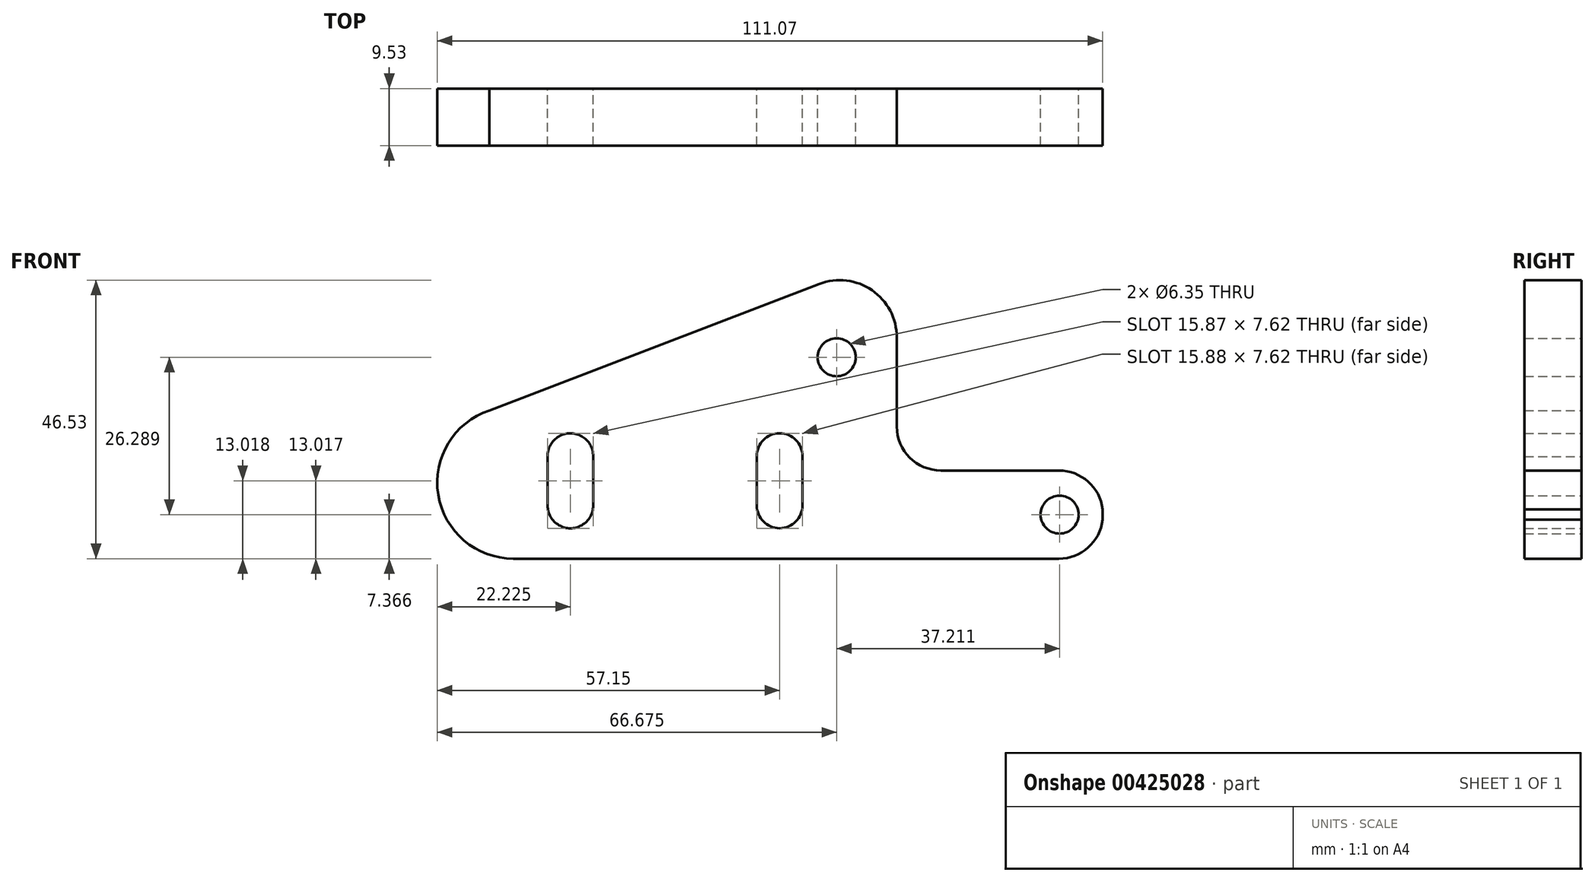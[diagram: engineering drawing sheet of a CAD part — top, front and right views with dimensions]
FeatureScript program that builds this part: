
annotation { "Feature Type Name" : "Feature", "Feature Type Description" : "" }
export const myFeature = defineFeature(function(context is Context, id is Id, definition is map)
    precondition{}
    {
        {
            var Q0;
            Q0=qCreatedBy(makeId("Front.planeOp"),FACE);
            var sketch = newSketch(context, id + "F0", { "sketchPlane" : qUnion([Q0])});
            skArc(sketch, "E0", {"start": v(-4, 12.06) * mm, "mid": v(-12.54, -2.02) * mm, "end": v(0, -12.7) * mm});
            skLineSegment(sketch, "E1", {"start": v(0, -12.7) * mm, "end": v(91.06, -12.7) * mm});
            skLineSegment(sketch, "E2", {"start": v(-5.1, 11.63) * mm, "end": v(51.07, 33.2) * mm});
            skArc(sketch, "E3", {"start": v(91.06, -12.7) * mm, "mid": v(98.43, -5.33) * mm, "end": v(91.06, 2.03) * mm});
            skLineSegment(sketch, "E4", {"start": v(-12.7, 37.63) * mm, "end": v(-12.7, -27.3) * mm, "construction": true});
            skLineSegment(sketch, "E5", {"start": v(98.43, 29.58) * mm, "end": v(98.43, -38.1) * mm, "construction": true});
            skLineSegment(sketch, "E6", {"start": v(91.06, 2.03) * mm, "end": v(71.37, 2.03) * mm});
            skArc(sketch, "E7", {"start": v(64, 9.4) * mm, "mid": v(66.17, 4.19) * mm, "end": v(71.37, 2.03) * mm});
            skLineSegment(sketch, "E8", {"start": v(64, 9.4) * mm, "end": v(64, 24.3) * mm});
            skLineSegment(sketch, "E9", {"start": v(71.37, 9.4) * mm, "end": v(64, 9.4) * mm, "construction": true});
            skPoint(sketch, "E10.visualSharp", {"position": v(64, 38.16) * mm});
            skArc(sketch, "E10.filletArc", {"start": v(64, 24.3) * mm, "mid": v(59.88, 32.15) * mm, "end": v(51.07, 33.2) * mm});
            skCircle(sketch, "E11", {"center": v(91.19, -5.33) * mm, "radius": 3.18 * mm});
            skCircle(sketch, "E12", {"center": v(53.98, 20.96) * mm, "radius": 3.18 * mm});
            skLineSegment(sketch, "E13.left", {"start": v(48.26, 4.45) * mm, "end": v(48.26, -3.8) * mm});
            skLineSegment(sketch, "E13.right", {"start": v(40.64, 4.45) * mm, "end": v(40.64, -3.8) * mm});
            skArc(sketch, "E14", {"start": v(48.26, 4.45) * mm, "mid": v(44.45, 8.26) * mm, "end": v(40.64, 4.45) * mm});
            skArc(sketch, "E15", {"start": v(40.64, -3.8) * mm, "mid": v(44.45, -7.62) * mm, "end": v(48.26, -3.8) * mm});
            skLineSegment(sketch, "E16", {"start": v(44.45, 4.45) * mm, "end": v(9.53, 4.44) * mm, "construction": true});
            skArc(sketch, "E17", {"start": v(13.34, 4.44) * mm, "mid": v(9.5, 8.25) * mm, "end": v(5.72, 4.38) * mm});
            skLineSegment(sketch, "E18", {"start": v(44.45, -3.8) * mm, "end": v(9.53, -3.8) * mm, "construction": true});
            skArc(sketch, "E19", {"start": v(5.72, -3.8) * mm, "mid": v(9.52, -7.62) * mm, "end": v(13.34, -3.8) * mm});
            skLineSegment(sketch, "E20", {"start": v(13.34, 4.44) * mm, "end": v(13.34, -3.8) * mm});
            skLineSegment(sketch, "E21", {"start": v(5.72, 4.5) * mm, "end": v(5.72, -3.8) * mm});
            skSolve(sketch);
        }
        {
            var Q0;
            Q0 = qSketchRegion(id + "F0", true);
            extrude(context, id + "F1", {"entities" : qUnion([Q0]), "depth" : 9.52 * mm});
        }
        {
            var Q0;
            Q0=makeQuery(id+"F1.opExtrude","CAP_FACE",FACE,{"disambiguationData":[OSD([sQuery(id+"F0.wireOp",EDGE,"E0"),sQuery(id+"F0.wireOp",EDGE,"E1"),sQuery(id+"F0.wireOp",EDGE,"E2"),sQuery(id+"F0.wireOp",EDGE,"E3"),sQuery(id+"F0.wireOp",EDGE,"E6"),sQuery(id+"F0.wireOp",EDGE,"E7"),sQuery(id+"F0.wireOp",EDGE,"E8"),sQuery(id+"F0.wireOp",EDGE,"E10.filletArc"),sQuery(id+"F0.wireOp",EDGE,"E11"),sQuery(id+"F0.wireOp",EDGE,"E12"),sQuery(id+"F0.wireOp",EDGE,"E13.left"),sQuery(id+"F0.wireOp",EDGE,"E13.right"),sQuery(id+"F0.wireOp",EDGE,"E14"),sQuery(id+"F0.wireOp",EDGE,"E15"),sQuery(id+"F0.wireOp",EDGE,"E17"),sQuery(id+"F0.wireOp",EDGE,"E19"),sQuery(id+"F0.wireOp",EDGE,"E20"),sQuery(id+"F0.wireOp",EDGE,"E21")])],"isStart":false});
            var sketch = newSketch(context, id + "F2", { "sketchPlane" : qUnion([Q0])});
            skLineSegment(sketch, "E22", {"start": v(98.43, -5.33) * mm, "end": v(98.37, -5.33) * mm});
            skPoint(sketch, "E22.endSnap0", {"position": v(98.43, -5.33) * mm});
            skLineSegment(sketch, "E23", {"start": v(98.37, -4.47) * mm, "end": v(98.37, -6.2) * mm});
            skArc(sketch, "E24.0", {"start": v(98.37, -6.2) * mm, "mid": v(98.43, -5.33) * mm, "end": v(98.37, -4.47) * mm});
            skPoint(sketch, "E25.orphan", {"position": v(91.06, 2.03) * mm});
            skPoint(sketch, "E26.orphan", {"position": v(91.06, -12.7) * mm});
            skSolve(sketch);
        }
        {
            var Q0;
            Q0 = qSketchRegion(id + "F2", true);
            extrude(context, id + "F3", {"entities" : qUnion([Q0]), "operationType" : NewBodyOperationType.REMOVE, "oppositeDirection" : true, "depth" : 127 * mm});
        }
    });
